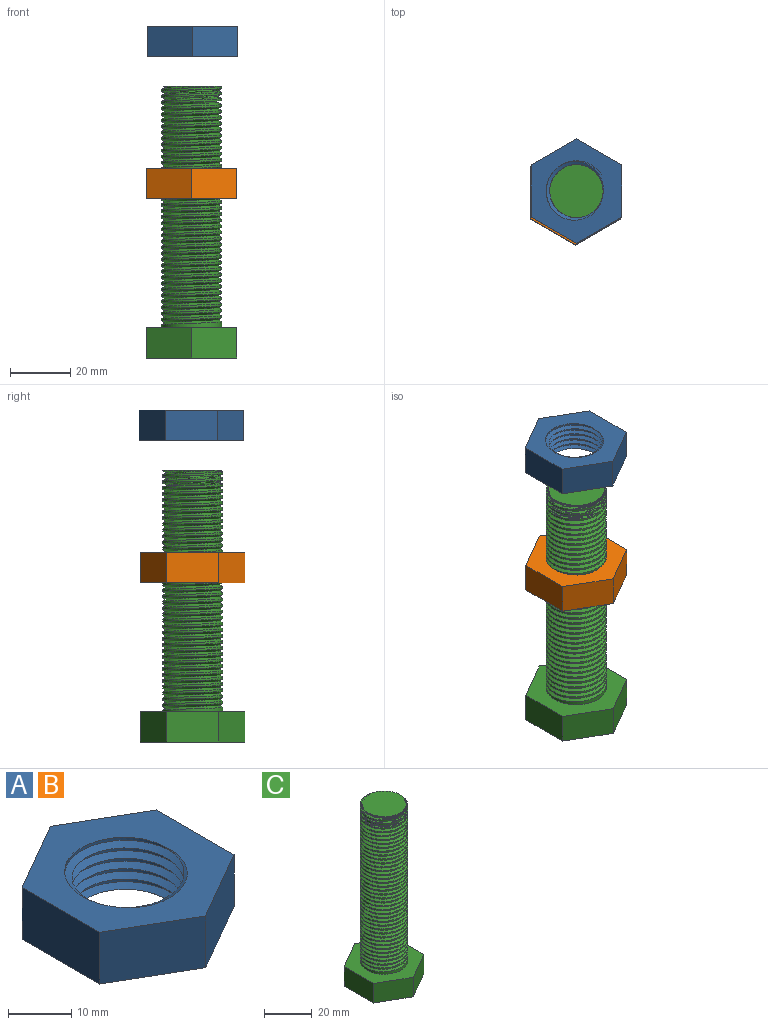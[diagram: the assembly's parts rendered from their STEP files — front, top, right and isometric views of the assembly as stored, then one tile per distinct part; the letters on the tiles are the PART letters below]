
ASSEMBLY  parts=3 mates=1
PART A: 11 faces, bbox 30.7x35.4x12.4 mm
  f0: plane 35.36x30.72mm, normal (0,0,-1), area 488.4mm2, adj f2,f3,f4,f5,f6,f7,f8,f9
  f1: plane 35.36x30.72mm, normal (0,0,1), area 488.4mm2, adj f2,f3,f4,f5,f6,f7,f8,f9
  f2: plane 17.32x10mm, normal (-1,0,0), area 173.2mm2, adj f0,f1,f3,f7
  f3: plane 15x10mm, normal (-0.5,-0.87,0), area 173.2mm2, adj f0,f1,f2,f4
  f4: plane 15x10mm, normal (0.5,-0.87,0), area 173.2mm2, adj f0,f1,f3,f5
  f5: plane 17.32x10mm, normal (1,0,0), area 173.2mm2, adj f0,f1,f4,f6
  f6: plane 15x10mm, normal (0.5,0.87,0), area 173.2mm2, adj f0,f1,f5,f7
  f7: plane 15x10mm, normal (-0.5,0.87,0), area 173.2mm2, adj f0,f1,f2,f6
  f8: cylinder r=10mm len=20mm, axis (0,0,-1), area 210.8mm2, adj f0,f1,f9,f10
  f9: bspline ~23.09x20mm, area 394.1mm2, adj f0,f1,f8,f10
  f10: bspline ~23.09x20mm, area 394.1mm2, adj f0,f1,f8,f9
PART B: same geometry as A
PART C: 13 faces, bbox 30.7x35.3x91.7 mm
  f0: plane 34.64x30mm, normal (0,0,1), area 465.3mm2, adj f1,f2,f3,f4,f5,f6,f8
  f1: plane 15x10mm, normal (-0.5,-0.87,0), area 173.2mm2, adj f0,f2,f6,f7
  f2: plane 15x10mm, normal (0.5,-0.87,0), area 173.2mm2, adj f0,f1,f3,f7
  f3: plane 17.32x10mm, normal (1,0,0), area 173.2mm2, adj f0,f2,f4,f7
  f4: plane 15x10mm, normal (0.5,0.87,0), area 173.2mm2, adj f0,f3,f5,f7
  f5: plane 15x10mm, normal (-0.5,0.87,0), area 173.2mm2, adj f0,f4,f6,f7
  f6: plane 17.32x10mm, normal (-1,0,0), area 173.2mm2, adj f0,f1,f5,f7
  f7: plane 34.64x30mm, normal (0,0,-1), area 779.4mm2, adj f1,f2,f3,f4,f5,f6
  f8: cylinder r=10mm len=80mm, axis (0,0,-1), area 3317.9mm2, adj f0,f9,f10,f11,f12
  f9: plane 20.11x19.83mm, normal (0,0,1), area 291mm2, adj f8,f11,f12
  f10: plane 1.33x1.15mm, normal (0,1,0), area 0.8mm2, adj f8,f11,f12
  f11: bspline ~80.67x23.09mm, area 3132mm2, adj f8,f9,f10,f12
  f12: bspline ~80.33x23.09mm, area 3102.1mm2, adj f8,f9,f10,f11
PLACE A rot(axis=(1,0,0),180deg) t=(-6.7,9.29,122.05)mm
PLACE B t=(-6.96,8.84,-20.65)mm
PLACE C t=(-6.96,8.84,-20.65)mm
MATE cylindrical A.f8 <-> C.f9  axis (0,0,-1) through (-6.7,9.29,69.35)mm
